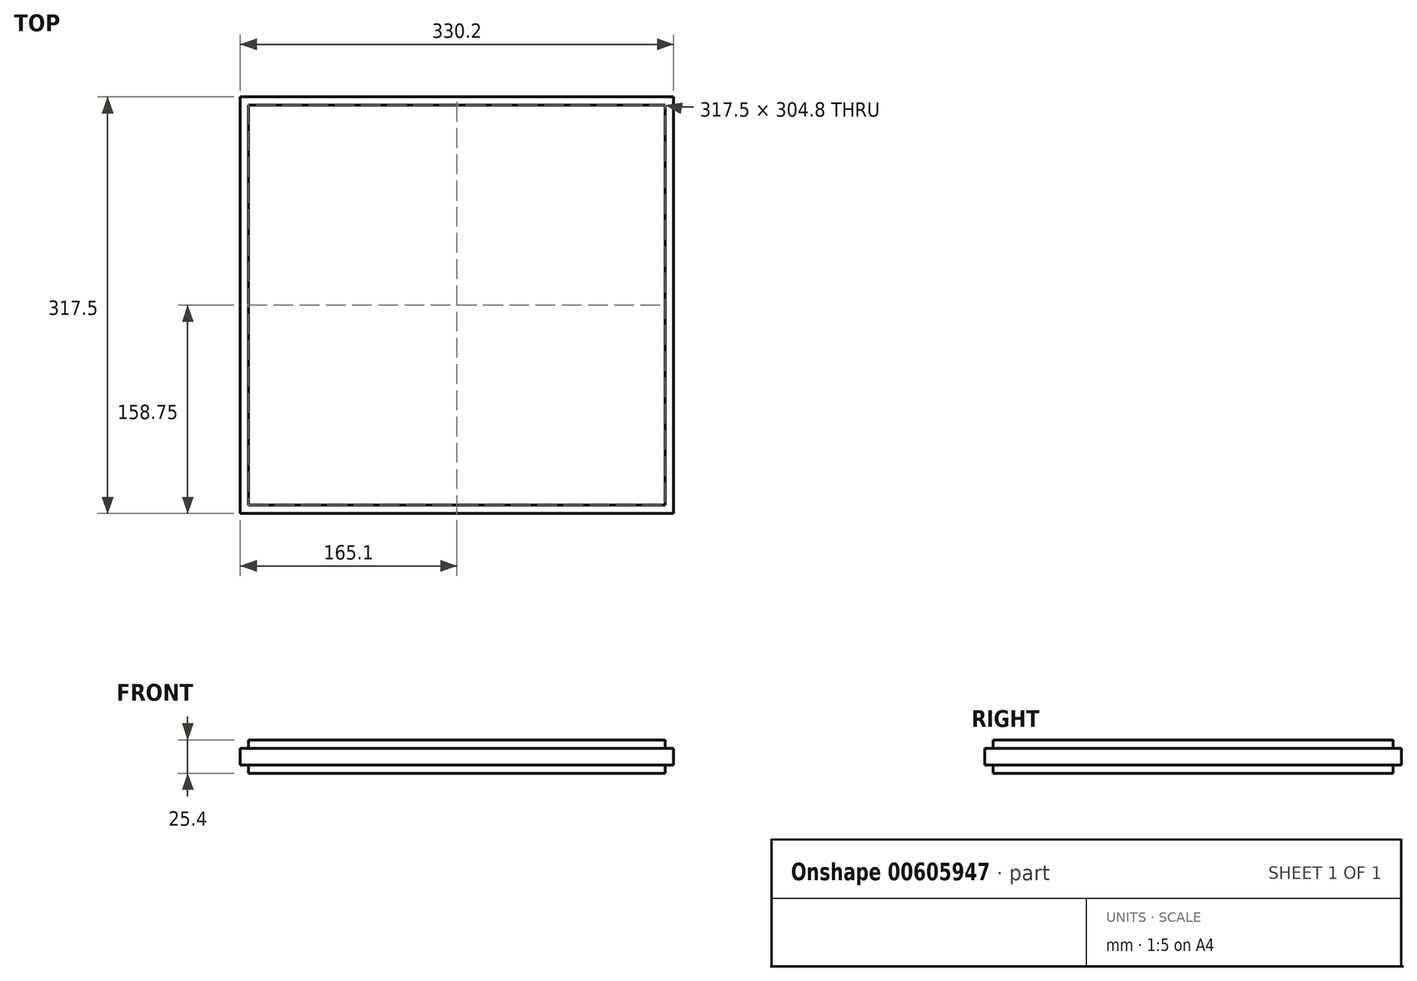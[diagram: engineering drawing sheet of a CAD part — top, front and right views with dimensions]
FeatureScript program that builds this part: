
annotation { "Feature Type Name" : "Feature", "Feature Type Description" : "" }
export const myFeature = defineFeature(function(context is Context, id is Id, definition is map)
    precondition{}
    {
        {
            var Q0;
            Q0=qCreatedBy(makeId("Top.planeOp"),FACE);
            var sketch = newSketch(context, id + "F0", { "sketchPlane" : qUnion([Q0])});
            skLineSegment(sketch, "E0.bottom", {"start": v(158.75, -152.4) * mm, "end": v(-158.75, -152.4) * mm});
            skLineSegment(sketch, "E0.top", {"start": v(158.75, 152.4) * mm, "end": v(-158.75, 152.4) * mm});
            skLineSegment(sketch, "E0.left", {"start": v(158.75, -152.4) * mm, "end": v(158.75, 152.4) * mm});
            skLineSegment(sketch, "E0.right", {"start": v(-158.75, -152.4) * mm, "end": v(-158.75, 152.4) * mm});
            skPoint(sketch, "E0.middle", {"position": v(0, 0) * mm});
            skSolve(sketch);
        }
        {
            var Q0;
            Q0=makeQuery(id+"F0.imprint","IMPRINT",FACE,{"disambiguationData":[TD([[makeQuery(id+"F0.imprint","IMPRINT",EDGE,{"derivedFrom":sQuery(id+"F0.wireOp",EDGE,"E0.bottom")}),-1.0]])]});
            extrude(context, id + "F1", {"entities" : qUnion([Q0]), "depth" : 25.4 * mm, "offsetDistance" : 25.4 * mm});
        }
        {
            var Q0;
            Q0=makeQuery(id+"F1.opExtrude","SWEPT_FACE",FACE,{"disambiguationData":[OSD([sQuery(id+"F0.wireOp",EDGE,"E0.bottom")])]});
            var sketch = newSketch(context, id + "F2", { "sketchPlane" : qUnion([Q0])});
            skLineSegment(sketch, "E1", {"start": v(-158.75, 0) * mm, "end": v(-158.75, 6.35) * mm});
            skLineSegment(sketch, "E2", {"start": v(-158.75, 6.35) * mm, "end": v(-158.75, 19.05) * mm});
            skLineSegment(sketch, "E3", {"start": v(-158.75, 19.05) * mm, "end": v(158.75, 19.05) * mm});
            skLineSegment(sketch, "E4", {"start": v(158.75, 19.05) * mm, "end": v(158.75, 6.35) * mm});
            skPoint(sketch, "E4.endSnap0", {"position": v(158.75, 12.7) * mm});
            skLineSegment(sketch, "E5", {"start": v(158.75, 6.35) * mm, "end": v(-158.75, 6.35) * mm});
            skSolve(sketch);
        }
        {
            var Q0;
            Q0=makeQuery(id+"F2.imprint","IMPRINT",FACE,{"disambiguationData":[TD([[makeQuery(id+"F2.imprint","IMPRINT",EDGE,{"derivedFrom":sQuery(id+"F2.wireOp",EDGE,"E2")}),1.0]])]});
            extrude(context, id + "F3", {"entities" : qUnion([Q0]), "operationType" : NewBodyOperationType.ADD, "depth" : 6.35 * mm, "offsetDistance" : 25.4 * mm});
        }
        {
            var Q0;
            Q0=makeQuery(id+"F1.opExtrude","SWEPT_FACE",FACE,{"disambiguationData":[OSD([sQuery(id+"F0.wireOp",EDGE,"E0.top")])]});
            var sketch = newSketch(context, id + "F4", { "sketchPlane" : qUnion([Q0])});
            skLineSegment(sketch, "E6", {"start": v(-158.75, 0) * mm, "end": v(-158.75, 6.35) * mm});
            skLineSegment(sketch, "E7", {"start": v(-158.75, 6.35) * mm, "end": v(-158.75, 19.05) * mm});
            skLineSegment(sketch, "E8", {"start": v(158.75, 19.05) * mm, "end": v(-158.75, 19.05) * mm});
            skPoint(sketch, "E8.startSnap0", {"position": v(158.75, 12.7) * mm});
            skLineSegment(sketch, "E9", {"start": v(158.75, 19.05) * mm, "end": v(158.75, 6.35) * mm});
            skLineSegment(sketch, "E10", {"start": v(158.75, 6.35) * mm, "end": v(-158.75, 6.35) * mm});
            skSolve(sketch);
        }
        {
            var Q0;
            Q0=makeQuery(id+"F4.imprint","IMPRINT",FACE,{"disambiguationData":[TD([[makeQuery(id+"F4.imprint","IMPRINT",EDGE,{"derivedFrom":sQuery(id+"F4.wireOp",EDGE,"E7")}),1.0]])]});
            extrude(context, id + "F5", {"entities" : qUnion([Q0]), "operationType" : NewBodyOperationType.ADD, "depth" : 6.35 * mm, "offsetDistance" : 25.4 * mm});
        }
        {
            var Q0;
            Q0=makeQuery(id+"F5.boolean.opBoolean","MERGE",FACE,{"derivedFrom":[makeQuery(id+"F3.boolean.opBoolean","MERGE",FACE,{"derivedFrom":[makeQuery(id+"F1.opExtrude","SWEPT_FACE",FACE,{"disambiguationData":[OSD([sQuery(id+"F0.wireOp",EDGE,"E0.right")])]}),makeQuery(id+"F3.opExtrude","SWEPT_FACE",FACE,{"disambiguationData":[OSD([sQuery(id+"F2.wireOp",EDGE,"E2")])]})]}),makeQuery(id+"F5.opExtrude","SWEPT_FACE",FACE,{"disambiguationData":[OSD([sQuery(id+"F4.wireOp",EDGE,"E9")])]})]});
            var sketch = newSketch(context, id + "F6", { "sketchPlane" : qUnion([Q0])});
            skLineSegment(sketch, "E11.bottom", {"start": v(-158.75, 19.05) * mm, "end": v(158.75, 19.05) * mm});
            skLineSegment(sketch, "E11.top", {"start": v(-158.75, 6.35) * mm, "end": v(158.75, 6.35) * mm});
            skLineSegment(sketch, "E11.left", {"start": v(-158.75, 19.05) * mm, "end": v(-158.75, 6.35) * mm});
            skLineSegment(sketch, "E11.right", {"start": v(158.75, 19.05) * mm, "end": v(158.75, 6.35) * mm});
            skSolve(sketch);
        }
        {
            var Q0;
            Q0=makeQuery(id+"F5.boolean.opBoolean","MERGE",FACE,{"derivedFrom":[makeQuery(id+"F3.boolean.opBoolean","MERGE",FACE,{"derivedFrom":[makeQuery(id+"F1.opExtrude","SWEPT_FACE",FACE,{"disambiguationData":[OSD([sQuery(id+"F0.wireOp",EDGE,"E0.left")])]}),makeQuery(id+"F3.opExtrude","SWEPT_FACE",FACE,{"disambiguationData":[OSD([sQuery(id+"F2.wireOp",EDGE,"E4")])]})]}),makeQuery(id+"F5.opExtrude","SWEPT_FACE",FACE,{"disambiguationData":[OSD([sQuery(id+"F4.wireOp",EDGE,"E7")])]})]});
            var sketch = newSketch(context, id + "F7", { "sketchPlane" : qUnion([Q0])});
            skLineSegment(sketch, "E12.bottom", {"start": v(-158.75, 19.05) * mm, "end": v(158.75, 19.05) * mm});
            skLineSegment(sketch, "E12.top", {"start": v(-158.75, 6.35) * mm, "end": v(158.75, 6.35) * mm});
            skLineSegment(sketch, "E12.left", {"start": v(-158.75, 19.05) * mm, "end": v(-158.75, 6.35) * mm});
            skLineSegment(sketch, "E12.right", {"start": v(158.75, 19.05) * mm, "end": v(158.75, 6.35) * mm});
            skSolve(sketch);
        }
        {
            var Q0;
            {var subQ15=sQuery(id+"F7.wireOp",EDGE,"E12.left");Q0=makeQuery(id+"F7.imprint","IMPRINT",FACE,{"disambiguationData":[TD([[makeQuery(id+"F7.imprint","IMPRINT",EDGE,{"derivedFrom":subQ15}),1.0]])]});}
            extrude(context, id + "F8", {"entities" : qUnion([Q0]), "operationType" : NewBodyOperationType.ADD, "depth" : 6.35 * mm, "offsetDistance" : 25.4 * mm});
        }
        {
            var Q0;
            {var subQ15=sQuery(id+"F6.wireOp",EDGE,"E11.left");Q0=makeQuery(id+"F6.imprint","IMPRINT",FACE,{"disambiguationData":[TD([[makeQuery(id+"F6.imprint","IMPRINT",EDGE,{"derivedFrom":subQ15}),1.0]])]});}
            extrude(context, id + "F9", {"entities" : qUnion([Q0]), "operationType" : NewBodyOperationType.ADD, "depth" : 6.35 * mm, "offsetDistance" : 25.4 * mm});
        }
    });
